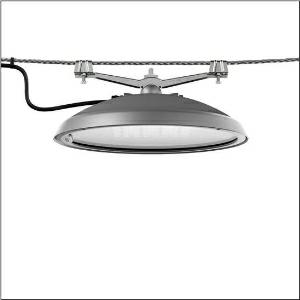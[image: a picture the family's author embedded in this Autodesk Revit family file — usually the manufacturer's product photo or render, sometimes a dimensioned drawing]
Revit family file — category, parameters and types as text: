
# Revit family: dl_50_iq_mini___st0_8s_5xa248v41f08ge_27a7
name_source: partatom
category: Lighting Fixtures
units: mm (PartAtom-declared; Revit-internal decimal feet)

## family parameters
Cut with Voids When Loaded = No
Host = Face
Light Source = No
Part Type = Normal
Room Calculation Point = No
Round Connector Dimension = Use Diameter
Shared = No

## types (1)
- --- (1 x LED, 5190 lm, 31.2 W, 4000K)
    Apparent Load = 31 VA
    CIE Flux Codes = 38 75 97 100 100
    Color Rendering = 70
    Color Temperature = 4000K
    Default Elevation = 1800 mm
    Description = DL 50 iQ mini, catenary luminaire, primary light control with lens, of PMMA, primary optical cover: cover, of toughened safety glass, transparent, light distribution: ST0.8s, light emission: direct distribution, primary light characteristic: symmetric, installation type: suspended mounting, LED, High Power LED, rated luminous flux: 5.190lm, luminous efficacy: 166lm/W, light colour: 740, colour temperature: 4000K, control gear: iQ Street-Remote, control: optimised constant luminous flux control (CLO 2.0), Desk-Remote (wireless, voltage-free reading and setting of iQ features in the workshop via application-optimized NFC function/RFID function), Light-Fading, Smart-Wire, Night-Set, Lumen-Switch, Temp-Guard, Auto-Match, Street-Remote, mains connection: 230..240V, AC, 50/60Hz, start of lifetime: 31W, end of service life: 32W, reduction: 15W, luminaire housing, of diecast aluminium, powder-coated, SITECO metallic grey (DB 702S), diameter: 500mm, height: 115mm, mounting height: 4..12m, protection rating (complete): IP66, insulation class (complete): insulation class II (safety insulation), certification: CE, ENEC, ENEC+, VDE, impact resistance: IK08, permissible operating ambient temperature for outdoor applications: -25..+40°C, standard-compliant lighting for roads and squares, packaging unit: 1 piece

Light Distribution: ST0.8s
    Height = 124 mm  [stored 0.406824 ft]
    Lamp = 1 x LED
    Lamp Light Flux = 5190 lm
    Lamp Power = 31.2 W
    Lamp count = 1
    Length = 500 mm
    Luminous efficacy = 166 lm/W
    Manufacturer = Siteco
    ModVariant = No
    Model = 5XA248V41F08GE
    Number of Poles = 1
    OnlyDefault = Yes
    Power Factor = 1
    Product Name = DL 50 iQ mini | ST0.8s
    Product group = catenary luminaire
    ProductGroupID = 6300
    Protection Class = Protection class II
    Protection Degree = IP 66
    RLX_Detail_Level = 1
    RLX_Emergency_Light_Flux = 0 lm
    RLX_Emergency_Type = 0
    RLX_Emergency_Type_DB = No
    RlxData = <blob elided: 123781 chars, md5=6d9b89c3>
    Socket = socket
    Standby Power = 0 W
    System Light Flux = 5190 lm
    System Power = 31 W
    Type Comments = factory setting: luminous flux: 100 % | dim-lin: 254 | 325 mA
    Type Image = l_1242791.jpg
    URL = http://relux.com
    VarID = @adj_140591
    Voltage = 0 V
    Weight = 0.00 kg
    Width = 0 mm  [stored 0 ft]

note: [stored X ft] marks values corroborated as IEEE doubles in the binary element streams (Revit-internal decimal feet)

## geometry (parser evidence)
native form markers: Blend x4, Sweep x13
no freeform markers — native parametric forms only
